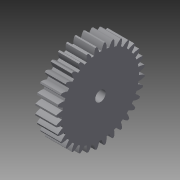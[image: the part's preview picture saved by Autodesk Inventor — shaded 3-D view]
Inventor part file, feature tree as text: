
AUTODESK INVENTOR PART (.ipt)
format: ipt  version: 2015 (Build 190159000, 159)  size: 323,072 bytes
history: native  units: in
note: dims shown in document units (in); Inventor stores cm internally (conversion verified against a paired STEP export)
features: other x1, extrude x1, imported_body x1, sketch x1
ambient origin geometry x8: Origin, YZ Plane, XZ Plane, XY Plane, X Axis, Y Axis, Z Axis, Center Point
bodies: Solid1 (feature_tree)
feature tree (4):
  other  "User Library-615290 32t Hitec pinion gear.sat1"
  extrude  "Extrusion1"  Depth=12.5984in TaperAngle=360.0deg
  imported_body  "Base1"
  sketch  "Sketch1"  dims[d0=0.2in d1=12.5984in d3=360.0deg d5=1.0in d6=0.0in]
